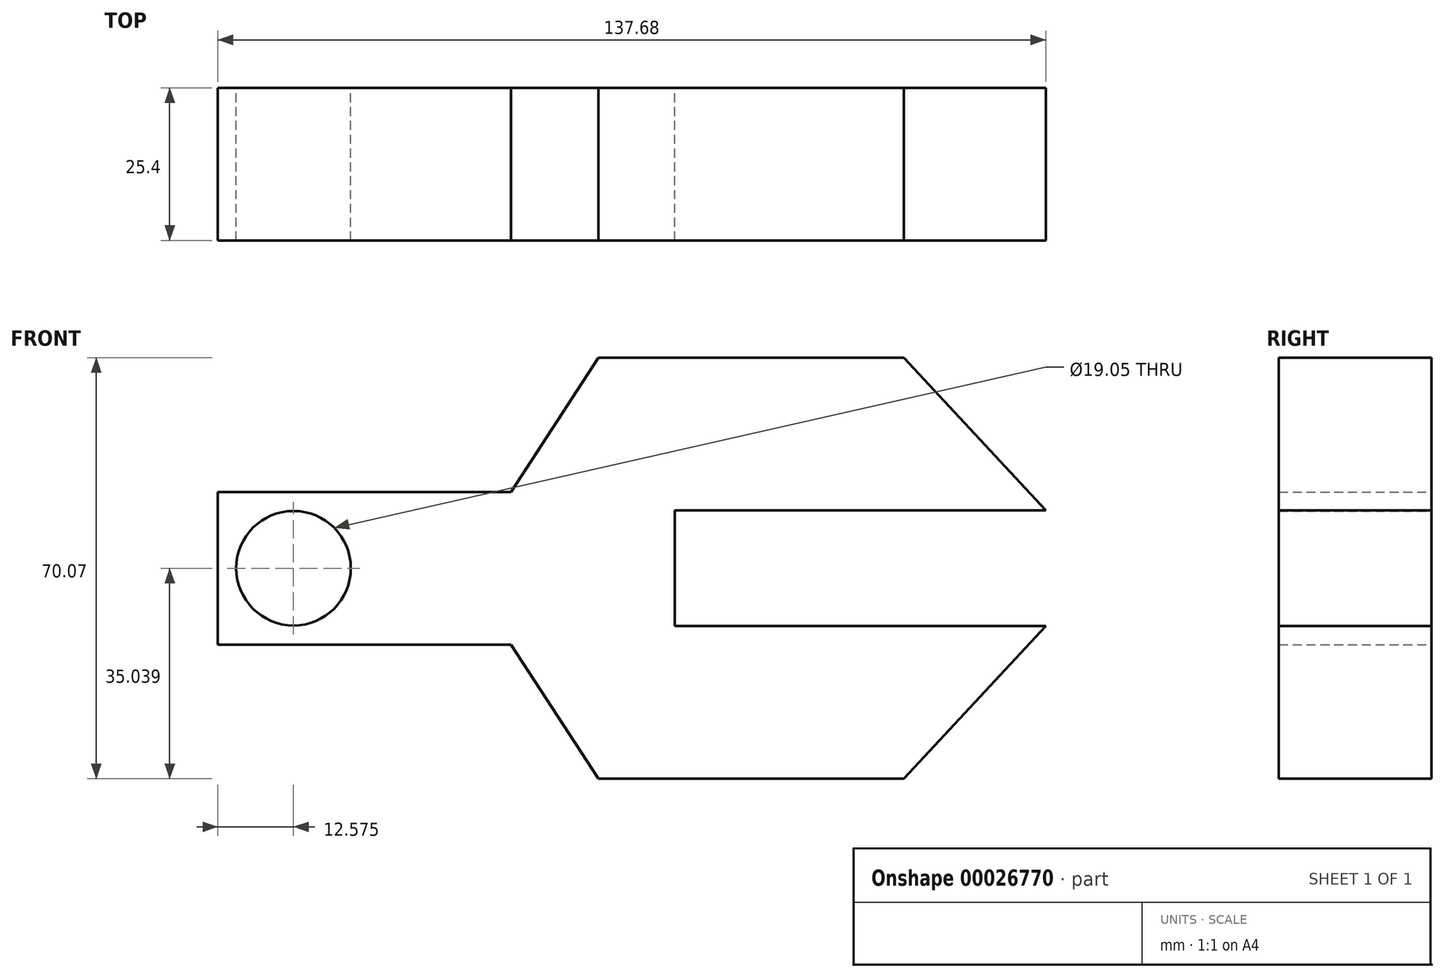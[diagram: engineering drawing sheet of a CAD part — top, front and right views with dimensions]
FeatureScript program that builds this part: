
annotation { "Feature Type Name" : "Feature", "Feature Type Description" : "" }
export const myFeature = defineFeature(function(context is Context, id is Id, definition is map)
    precondition{}
    {
        {
            var Q0;
            Q0=qCreatedBy(makeId("Front.planeOp"),FACE);
            var sketch = newSketch(context, id + "F0", { "sketchPlane" : qUnion([Q0])});
            skLineSegment(sketch, "E0.bottom", {"start": v(-79.88, 19.68) * mm, "end": v(-31.14, 19.68) * mm});
            skLineSegment(sketch, "E0.top", {"start": v(-79.88, -5.72) * mm, "end": v(-31.14, -5.72) * mm});
            skLineSegment(sketch, "E0.left", {"start": v(-79.88, 19.68) * mm, "end": v(-79.88, -5.72) * mm});
            skLineSegment(sketch, "E0.right", {"start": v(-31.14, 19.68) * mm, "end": v(-31.14, -5.72) * mm});
            skLineSegment(sketch, "E1", {"start": v(-31.14, 19.68) * mm, "end": v(-16.57, 42) * mm});
            skLineSegment(sketch, "E2", {"start": v(-16.57, 42) * mm, "end": v(34.23, 42) * mm});
            skLineSegment(sketch, "E3", {"start": v(34.23, 42) * mm, "end": v(57.8, 16.6) * mm});
            skLineSegment(sketch, "E4", {"start": v(57.8, 16.6) * mm, "end": v(-3.89, 16.6) * mm});
            skLineSegment(sketch, "E5", {"start": v(-3.89, 16.6) * mm, "end": v(-3.89, -2.66) * mm});
            skLineSegment(sketch, "E6", {"start": v(-3.89, -2.66) * mm, "end": v(57.8, -2.66) * mm});
            skLineSegment(sketch, "E7", {"start": v(57.8, -2.66) * mm, "end": v(34.23, -28.06) * mm});
            skLineSegment(sketch, "E8", {"start": v(34.23, -28.06) * mm, "end": v(-16.57, -28.06) * mm});
            skLineSegment(sketch, "E9", {"start": v(-16.57, -28.06) * mm, "end": v(-31.14, -5.72) * mm});
            skPoint(sketch, "E10", {"position": v(-79.88, 6.98) * mm});
            skCircle(sketch, "E11", {"center": v(-67.3, 6.98) * mm, "radius": 9.53 * mm});
            skSolve(sketch);
        }
        {
            var Q0;
            Q0 = qSketchRegion(id + "F0", true);
            extrude(context, id + "F1", {"entities" : qUnion([Q0]), "depth" : 25.4 * mm});
        }
    });
